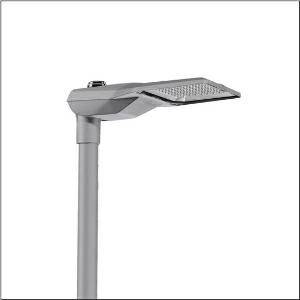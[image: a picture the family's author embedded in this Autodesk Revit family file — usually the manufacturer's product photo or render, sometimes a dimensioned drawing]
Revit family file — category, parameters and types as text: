
# Revit family: streetlight_sl_21_midi___p1_0a_5xe7a37n08lb_cb5e
name_source: partatom
category: Lighting Fixtures
units: mm (PartAtom-declared; Revit-internal decimal feet)

## family parameters
Cut with Voids When Loaded = No
Host = Face
Light Source = No
Part Type = Normal
Room Calculation Point = No
Round Connector Dimension = Use Diameter
Shared = No

## types (1)
- --- (1 x LED, 14340 lm, 98.3 W, 3000K)
    Apparent Load = 98 VA
    CIE Flux Codes = 21 50 90 100 100
    Color Rendering = 70
    Color Temperature = 3000K
    Default Elevation = 1800 mm
    Description = Streetlight SL 21 midi, mast luminaire, primary light control with lens, of PMMA, primary optical cover: cover, of toughened safety glass, transparent, light distribution: P1.0a, light emission: direct distribution, primary light characteristic: asymmetric, installation type: side-entry, LED, 3G 2.5mm², High Power LED, rated luminous flux: 14.340lm, luminous efficacy: 146lm/W, light colour: 730, colour temperature: 3000K, control: overheat protection, presetting dimming linear, constant luminous flux control, time-dependent luminous flux control, flexible luminous flux parameterisation, mains connection: 220..240V, AC, 50/60Hz, connection cable pre-assembled, cable length: 10,5m, wiring characteristics: H05VV-F, start of lifetime: 98W, end of service life: 101W, reduction: 45W, luminaire housing, of diecast aluminium (EN AC-44300), powder-coated, Siteco® metallic grey (DB 702S), corrosivity category C5 mid according to DIN EN ISO 12944, multi-level sealing system, sealing non-destructively replaceable, inclination adjustable: 0°, 5°, 10°, 15°, length: 644mm, width: 335mm, height: 110mm, spigot size: 42mm (side-entry), protection rating (complete): IP66, insulation class (complete): insulation class I (protective earthing), certification: CE, ENEC, ENEC+, VDE, impact resistance: IK09, permissible operating ambient temperature for outdoor applications: -40..+50°C, standard-compliant lighting for roads and squares, packaging unit: 1 piece

Light Distribution: P1.0a
    Height = 111 mm
    Lamp = 1 x LED
    Lamp Light Flux = 14340 lm
    Lamp Power = 98.3 W
    Lamp count = 1
    Length = 644 mm
    Luminous efficacy = 146 lm/W
    Manufacturer = Siteco
    ModVariant = No
    Model = 5XE7A37N08LB
    Number of Poles = 1
    OnlyDefault = Yes
    Power Factor = 1
    Product Name = Streetlight SL 21 midi | P1.0a
    Product group = mast luminaire | pylon top
    ProductGroupID = 6100
    Protection Class = Protection class I
    Protection Degree = IP 66
    RLX_Detail_Level = 1
    RLX_Emergency_Light_Flux = 0 lm
    RLX_Emergency_Type = 0
    RLX_Emergency_Type_DB = No
    RlxData = <blob elided: 101605 chars, md5=64aa71f6>
    Socket = socket
    Standby Power = 0 W
    System Light Flux = 14340 lm
    System Power = 98 W
    Type Comments = factory setting: luminous flux: 100 % | dim-lin: 254 | 1020 mA
    Type Image = l_1294377.jpg
    URL = http://relux.com
    VarID = @adj_065893
    Voltage = 0 V
    Weight = 0.00 kg
    Width = 336 mm

## geometry (parser evidence)
native form markers: Blend x4, Sweep x9
no freeform markers — native parametric forms only
